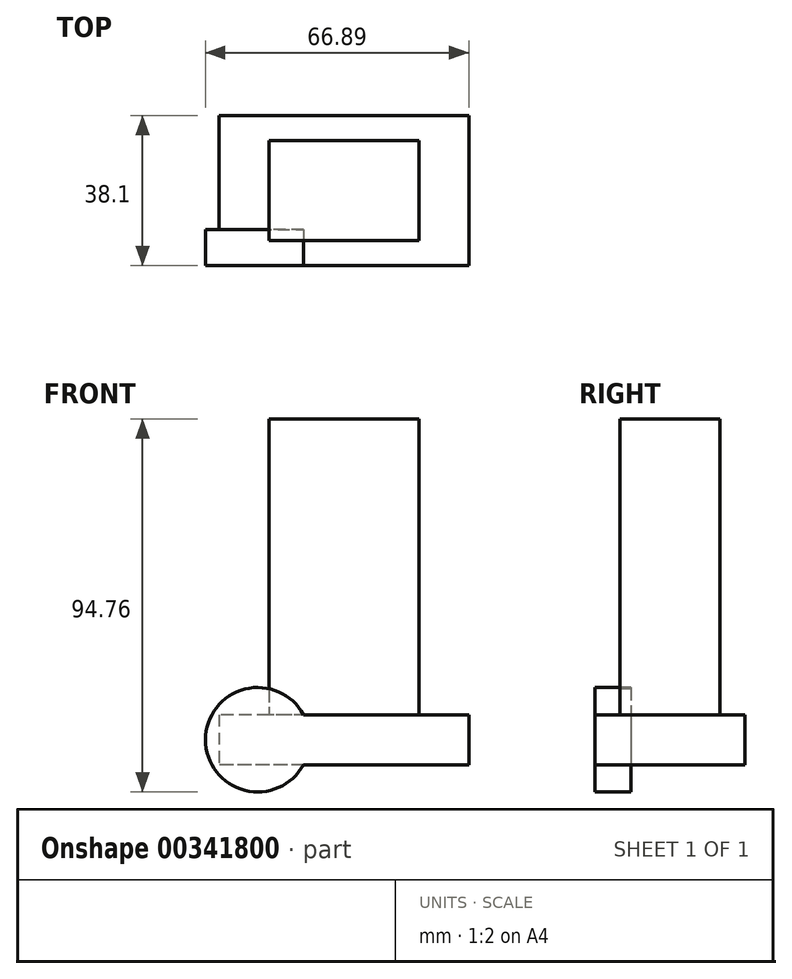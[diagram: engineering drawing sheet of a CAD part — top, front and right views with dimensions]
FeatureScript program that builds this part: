
annotation { "Feature Type Name" : "Feature", "Feature Type Description" : "" }
export const myFeature = defineFeature(function(context is Context, id is Id, definition is map)
    precondition{}
    {
        {
            var Q0;
            Q0=qCreatedBy(makeId("Top.planeOp"),FACE);
            var sketch = newSketch(context, id + "F0", { "sketchPlane" : qUnion([Q0])});
            skLineSegment(sketch, "E0.bottom", {"start": v(31.75, 19.05) * mm, "end": v(-31.75, 19.05) * mm});
            skLineSegment(sketch, "E0.top", {"start": v(31.75, -19.05) * mm, "end": v(-31.75, -19.05) * mm});
            skLineSegment(sketch, "E0.left", {"start": v(31.75, 19.05) * mm, "end": v(31.75, -19.05) * mm});
            skLineSegment(sketch, "E0.right", {"start": v(-31.75, 19.05) * mm, "end": v(-31.75, -19.05) * mm});
            skPoint(sketch, "E0.middle", {"position": v(0, 0) * mm});
            skSolve(sketch);
        }
        {
            var Q0;
            Q0 = qSketchRegion(id + "F0", true);
            extrude(context, id + "F1", {"entities" : qUnion([Q0]), "endBound" : BoundingType.SYMMETRIC, "depth" : 12.7 * mm});
        }
        {
            var Q0;
            Q0=makeQuery(id+"F1.opExtrude","CAP_FACE",FACE,{"disambiguationData":[OSD([sQuery(id+"F0.wireOp",EDGE,"E0.bottom"),sQuery(id+"F0.wireOp",EDGE,"E0.top"),sQuery(id+"F0.wireOp",EDGE,"E0.left"),sQuery(id+"F0.wireOp",EDGE,"E0.right")])],"isStart":false});
            var sketch = newSketch(context, id + "F2", { "sketchPlane" : qUnion([Q0])});
            skPoint(sketch, "E1.middle", {"position": v(0, 0) * mm});
            skLineSegment(sketch, "E2.bottom", {"start": v(19.05, 12.7) * mm, "end": v(-19.05, 12.7) * mm});
            skLineSegment(sketch, "E2.top", {"start": v(19.05, -12.7) * mm, "end": v(-19.05, -12.7) * mm});
            skLineSegment(sketch, "E2.left", {"start": v(19.05, 12.7) * mm, "end": v(19.05, -12.7) * mm});
            skLineSegment(sketch, "E2.right", {"start": v(-19.05, 12.7) * mm, "end": v(-19.05, -12.7) * mm});
            skSolve(sketch);
        }
        {
            var Q0;
            Q0 = qSketchRegion(id + "F2", true);
            extrude(context, id + "F3", {"entities" : qUnion([Q0]), "operationType" : NewBodyOperationType.ADD, "endBound" : BoundingType.THROUGH_ALL, "depth" : 25.4 * mm});
        }
        {
            var Q0;
            Q0=makeQuery(id+"F1.opExtrude","SWEPT_FACE",FACE,{"disambiguationData":[OSD([sQuery(id+"F0.wireOp",EDGE,"E0.top")])]});
            var sketch = newSketch(context, id + "F4", { "sketchPlane" : qUnion([Q0])});
            skCircle(sketch, "E3", {"center": v(-21.87, 0) * mm, "radius": 13.27 * mm});
            skSolve(sketch);
        }
        {
            var Q0;
            {var subQ1=sQuery(id+"F0.wireOp",EDGE,"E0.top");var subQ6=makeQuery(id+"F1.opExtrude","SWEPT_EDGE",EDGE,{"disambiguationData":[OSD([subQ1,sQuery(id+"F0.wireOp",EDGE,"E0.right")])]});Q0=makeQuery(id+"F4.imprint","IMPRINT",FACE,{"disambiguationData":[TD([[makeQuery(id+"F4.imprint","IMPRINT",EDGE,{"derivedFrom":subQ6}),-1.0]])]});}
            var Q1;
            Q1=sQuery(id+"F4.wireOp",EDGE,"E3");
            extrude(context, id + "F5", {"entities" : qUnion([Q0]), "operationType" : NewBodyOperationType.ADD, "surfaceEntities" : qUnion([Q1]), "oppositeDirection" : true, "depth" : 9.14 * mm});
        }
    });
